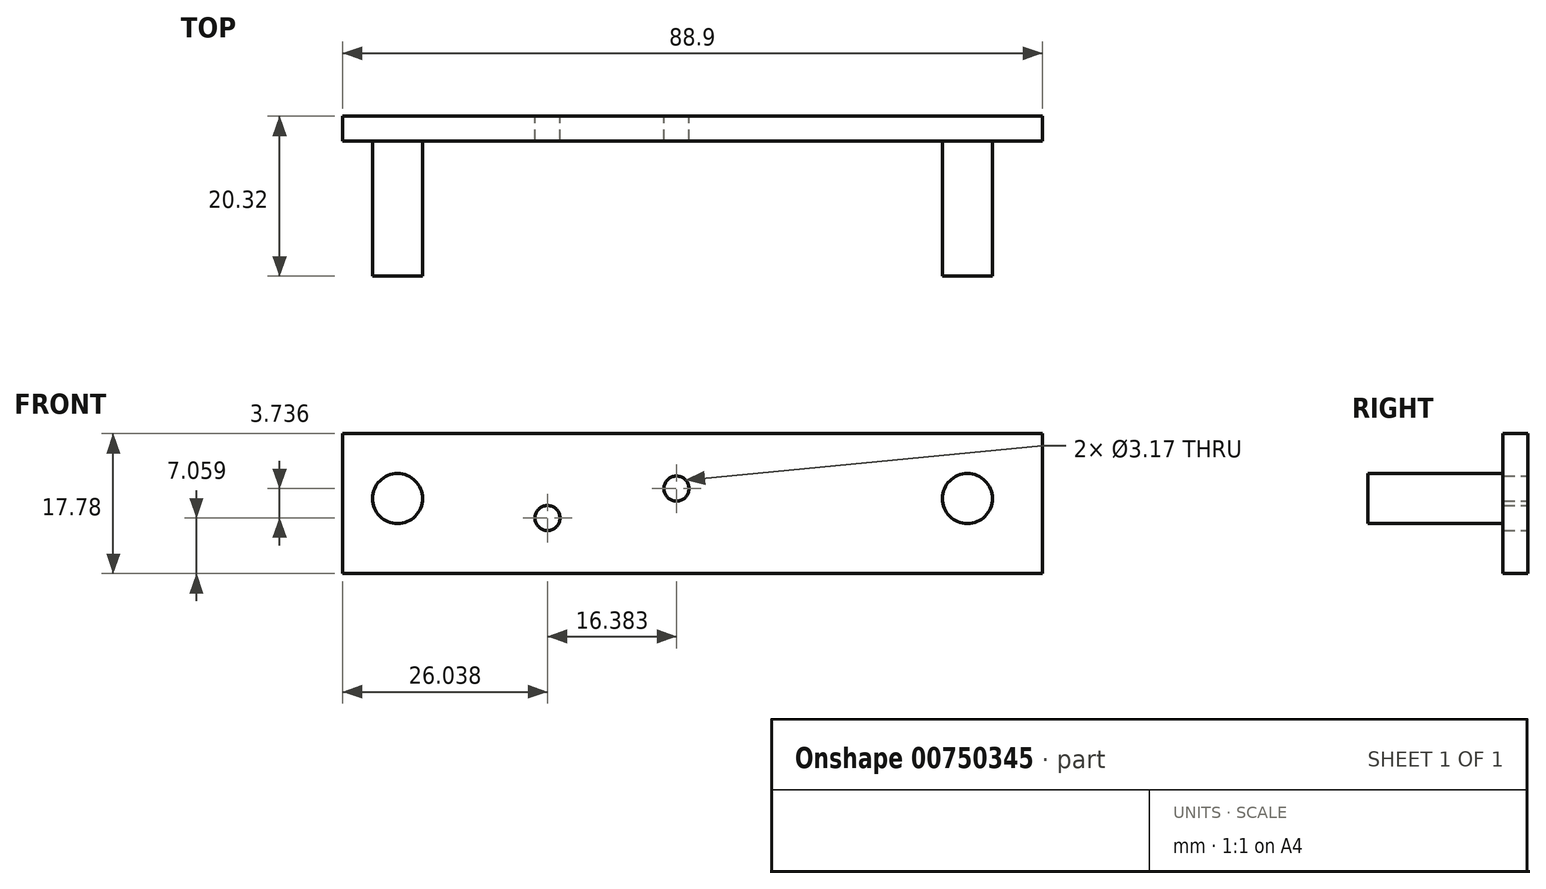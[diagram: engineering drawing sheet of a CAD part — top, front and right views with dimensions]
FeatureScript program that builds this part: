
annotation { "Feature Type Name" : "Feature", "Feature Type Description" : "" }
export const myFeature = defineFeature(function(context is Context, id is Id, definition is map)
    precondition{}
    {
        {
            var Q0;
            Q0=qCreatedBy(makeId("Front.planeOp"),FACE);
            var sketch = newSketch(context, id + "F0", { "sketchPlane" : qUnion([Q0])});
            skLineSegment(sketch, "E0.bottom", {"start": v(-44.67, -18.4) * mm, "end": v(44.23, -18.4) * mm});
            skLineSegment(sketch, "E0.top", {"start": v(-44.67, -36.19) * mm, "end": v(44.23, -36.19) * mm});
            skLineSegment(sketch, "E0.left", {"start": v(-44.67, -18.4) * mm, "end": v(-44.67, -36.19) * mm});
            skLineSegment(sketch, "E0.right", {"start": v(44.23, -18.4) * mm, "end": v(44.23, -36.19) * mm});
            skCircle(sketch, "E1", {"center": v(-2.25, -25.4) * mm, "radius": 1.59 * mm});
            skCircle(sketch, "E2", {"center": v(-37.68, -26.66) * mm, "radius": 3.18 * mm});
            skCircle(sketch, "E3", {"center": v(34.7, -26.66) * mm, "radius": 3.18 * mm});
            skCircle(sketch, "E4", {"center": v(-18.63, -29.13) * mm, "radius": 1.59 * mm});
            skSolve(sketch);
        }
        {
            var Q0;
            Q0 = qSketchRegion(id + "F0", true);
            extrude(context, id + "F1", {"entities" : qUnion([Q0]), "depth" : 3.17 * mm, "offsetDistance" : 25.4 * mm});
        }
        {
            var Q0;
            Q0=makeQuery(id+"F1.opExtrude","CAP_FACE",FACE,{"disambiguationData":[OSD([sQuery(id+"F0.wireOp",EDGE,"E0.bottom"),sQuery(id+"F0.wireOp",EDGE,"E0.top"),sQuery(id+"F0.wireOp",EDGE,"E0.left"),sQuery(id+"F0.wireOp",EDGE,"E0.right"),sQuery(id+"F0.wireOp",EDGE,"E1"),sQuery(id+"F0.wireOp",EDGE,"E2"),sQuery(id+"F0.wireOp",EDGE,"E3"),sQuery(id+"F0.wireOp",EDGE,"E4")])],"isStart":true});
            var sketch = newSketch(context, id + "F2", { "sketchPlane" : qUnion([Q0])});
            skCircle(sketch, "E5", {"center": v(-34.7, -26.66) * mm, "radius": 3.18 * mm});
            skCircle(sketch, "E6", {"center": v(37.68, -26.66) * mm, "radius": 3.18 * mm});
            skSolve(sketch);
        }
        {
            var Q0;
            Q0 = qSketchRegion(id + "F2", true);
            extrude(context, id + "F3", {"entities" : qUnion([Q0]), "operationType" : NewBodyOperationType.ADD, "oppositeDirection" : true, "depth" : 20.32 * mm, "offsetDistance" : 25.4 * mm});
        }
    });
